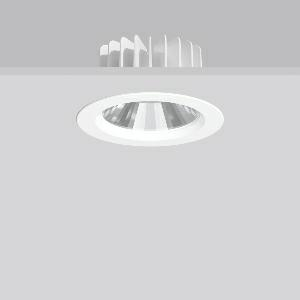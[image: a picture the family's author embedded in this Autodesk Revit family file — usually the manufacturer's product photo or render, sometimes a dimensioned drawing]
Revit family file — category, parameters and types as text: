
# Revit family: ledona_round_ip65_901793_002_1ef0
name_source: partatom
category: Lighting Fixtures
units: mm (PartAtom-declared; Revit-internal decimal feet)

## family parameters
Cut with Voids When Loaded = No
Host = Face
Light Source = No
Part Type = Normal
Room Calculation Point = No
Round Connector Dimension = Use Diameter
Shared = No

## types (1)
- MultiLumen 1 (1 x LED Modul 930, 1450 lm, 3000)
    Apparent Load = 12 VA
    Approval mark = CE
    CIE Flux Codes = 94 99 100 100 100
    Color Rendering = 90
    Color Temperature = 3000
    Default Elevation = 1800 mm
    Height = 0 mm  [stored 0 ft]
    Lamp = 1 x LED Modul 930
    Lamp Light Flux = 1450 lm
    Lamp count = 1
    Length = 140 mm  [stored 0.459318 ft]
    Lifetime = 50000 h
    Luminous efficacy = 121 lm/W
    Manufacturer = RZB
    ModVariant = No
    Model = 901793.002
    Mounting Place = Ceiling
    Mounting Type = Recessed
    Number of Poles = 1
    OnlyDefault = Yes
    Power Factor = 1
    Product Name = LEDONA round IP65
    Product group = Recessed downlights
    ProductGroupID = 402
    Protection Class = Protection class II
    Protection Degree = IP 65
    RLX_Detail_Level = 1
    RLX_Emergency_Light_Flux = 0 lm
    RLX_Emergency_Type = 0
    RLX_Emergency_Type_DB = No
    RlxData = <blob elided: 39141 chars, md5=22878acb>
    Socket = socket
    Standby Power = 0 W
    System Light Flux = 1450 lm
    System Power = 12 W
    Type Comments = MultiLumen 1
    Type Image = 901346.002.jpg
    URL = http://relux.com
    VarID = multilumen_1
    Voltage = 230 V
    Voltage Range = 220-240 V
    Weight = 0.00 kg
    Width = 0 mm  [stored 0 ft]

note: [stored X ft] marks values corroborated as IEEE doubles in the binary element streams (Revit-internal decimal feet)

## geometry (parser evidence)
native form markers: Blend x4, Sweep x11
no freeform markers — native parametric forms only
